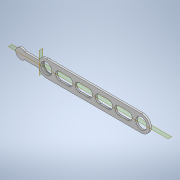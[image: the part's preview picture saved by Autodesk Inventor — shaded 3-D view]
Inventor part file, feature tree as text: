
AUTODESK INVENTOR PART (.ipt)
format: ipt  version: 2022 (Build 260153000, 153)  size: 206,336 bytes
history: native  units: mm
features: sketch x3, extrude x3, plane x2, pattern_circular x1, other x1
ambient origin geometry x8: Origin, YZ Plane, XZ Plane, XY Plane, X Axis, Y Axis, Z Axis, Center Point
bodies: Body1 (feature_tree)
feature tree (10):
  sketch  "Sketch2"  dims[d27=170.0mm d28=30.0mm]
  extrude  "Extrusion2"  Depth=30.0mm
  extrude  "Extrusion3"  Depth=20.0mm
  plane  "Work Plane1"
  sketch  "Sketch4"  dims[d29=20.0mm d30=20.0mm]
  plane  "Work Plane2"
  extrude  "Extrusion5"  Depth=10.0mm
  pattern_circular  "Circular Pattern1"  Count=2  [1 undecoded]
  other  "Work Axis3"
  sketch  "Sketch5"  dims[d31=16.0mm d32=15.0mm d41=20.0mm d43=35.0mm d44=10.0mm d46=10.0mm d48=40.0mm d49=3.0mm d50=0.0mm d51=25.0mm d52=3.0mm d53=0.0mm d57=2.0mm d62=90.0deg d63=0.5mm d64=2.0mm d65=0.0mm d66=30.0mm d67=360.0deg]
note: 1 required parameter value undecoded (feature->parameter linkage not recoverable at this tier; creation-order binding heuristic only, values carry confidence <= 0.55)
